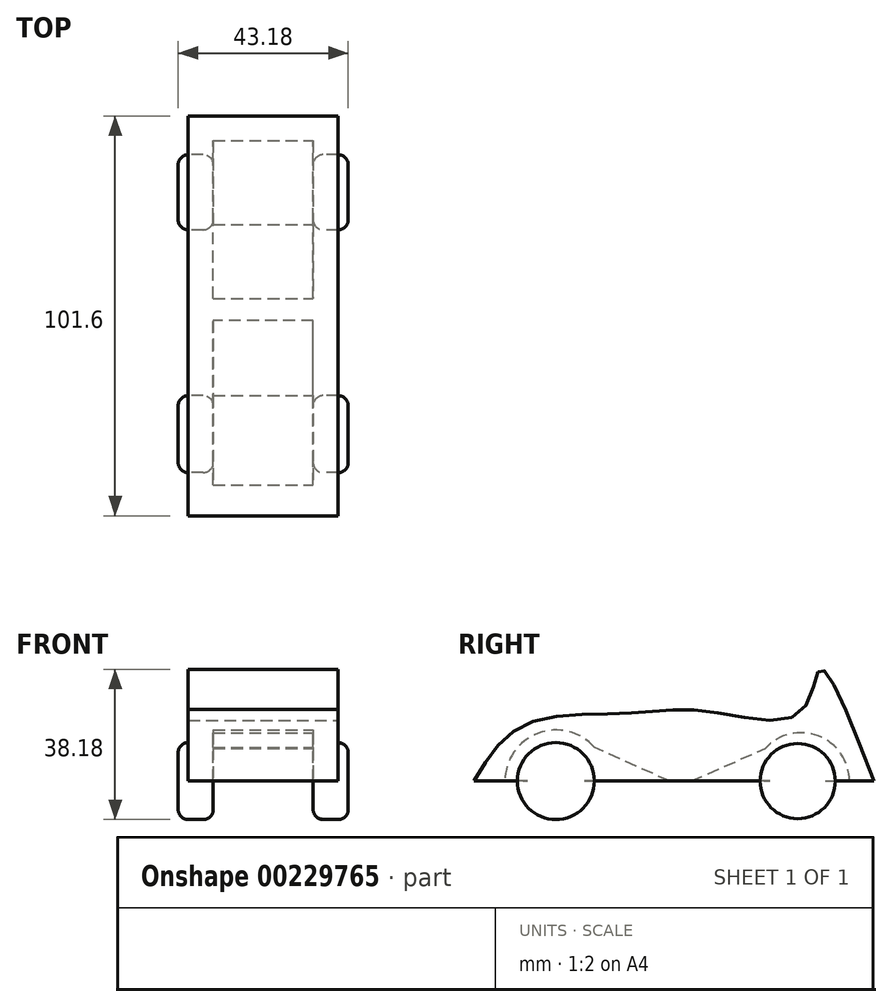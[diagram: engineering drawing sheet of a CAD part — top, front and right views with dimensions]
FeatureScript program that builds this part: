
annotation { "Feature Type Name" : "Feature", "Feature Type Description" : "" }
export const myFeature = defineFeature(function(context is Context, id is Id, definition is map)
    precondition{}
    {
        {
            var Q0;
            Q0=qCreatedBy(makeId("Right.planeOp"),FACE);
            var sketch = newSketch(context, id + "F0", { "sketchPlane" : qUnion([Q0])});
            skFitSpline(sketch, "E0", {"points": [v(-39.12, 0) * mm, v(-26.28, 14.3) * mm, v(0, 17.23) * mm, v(19.56, 17.8) * mm, v(43.8, 17.52) * mm, v(48.76, 28.32) * mm, v(62.48, 0) * mm], "startDerivative": vector(64.44, 109.87) * mm, "endDerivative": vector(84.94, -221.55) * mm});
            skLineSegment(sketch, "E1", {"start": v(-39.12, 0) * mm, "end": v(62.48, 0) * mm});
            skSolve(sketch);
        }
        {
            var Q0;
            Q0=qCreatedBy(makeId("Right.planeOp"),FACE);
            var sketch = newSketch(context, id + "F1", { "sketchPlane" : qUnion([Q0])});
            skCircle(sketch, "E2", {"center": v(-18.37, 0) * mm, "radius": 9.78 * mm});
            skCircle(sketch, "E3", {"center": v(43.09, 0) * mm, "radius": 9.55 * mm});
            skSolve(sketch);
        }
        {
            var Q0;
            Q0=makeQuery(id+"F0.imprint","IMPRINT",FACE,{"disambiguationData":[TD([[makeQuery(id+"F0.imprint","IMPRINT",EDGE,{"derivedFrom":sQuery(id+"F0.wireOp",EDGE,"E0")}),-1.0]])]});
            extrude(context, id + "F2", {"entities" : qUnion([Q0]), "endBound" : BoundingType.SYMMETRIC, "depth" : 38.1 * mm});
        }
        {
            var Q0;
            Q0=makeQuery(id+"F1.imprint","IMPRINT",FACE,{"disambiguationData":[TD([[makeQuery(id+"F1.imprint","IMPRINT",EDGE,{"derivedFrom":sQuery(id+"F1.wireOp",EDGE,"E2")}),1.0]])]});
            var Q1;
            Q1=makeQuery(id+"F1.imprint","IMPRINT",FACE,{"disambiguationData":[TD([[makeQuery(id+"F1.imprint","IMPRINT",EDGE,{"derivedFrom":sQuery(id+"F1.wireOp",EDGE,"E3")}),1.0]])]});
            extrude(context, id + "F3", {"entities" : qUnion([Q0, Q1]), "operationType" : NewBodyOperationType.ADD, "endBound" : BoundingType.SYMMETRIC, "depth" : 43.18 * mm});
        }
        {
            var Q0;
            Q0=makeQuery(id+"F3.opExtrude","CAP_EDGE",EDGE,{"disambiguationData":[OSD([sQuery(id+"F1.wireOp",EDGE,"E2")])],"isStart":false});
            var Q1;
            Q1=makeQuery(id+"F3.opExtrude","CAP_EDGE",EDGE,{"disambiguationData":[OSD([sQuery(id+"F1.wireOp",EDGE,"E3")])],"isStart":false});
            var Q2;
            Q2=makeQuery(id+"F3.opExtrude","CAP_EDGE",EDGE,{"disambiguationData":[OSD([sQuery(id+"F1.wireOp",EDGE,"E2")])],"isStart":true});
            var Q3;
            Q3=makeQuery(id+"F3.opExtrude","CAP_EDGE",EDGE,{"disambiguationData":[OSD([sQuery(id+"F1.wireOp",EDGE,"E3")])],"isStart":true});
            fillet(context, id + "F4", {"entities" : qUnion([Q0, Q1, Q2, Q3]), "radius" : 2.54 * mm, "tangentPropagation" : true, "allowEdgeOverflow" : false});
        }
        {
            var Q0;
            Q0=qCreatedBy(makeId("Right.planeOp"),FACE);
            var sketch = newSketch(context, id + "F5", { "sketchPlane" : qUnion([Q0])});
            skCircle(sketch, "E4", {"center": v(-18.29, 0) * mm, "radius": 12.97 * mm});
            skCircle(sketch, "E5", {"center": v(43.92, 0) * mm, "radius": 12.29 * mm});
            skSolve(sketch);
        }
        {
            var Q0;
            Q0=makeQuery(id+"F5.imprint","IMPRINT",FACE,{"disambiguationData":[TD([[makeQuery(id+"F5.imprint","IMPRINT",EDGE,{"derivedFrom":sQuery(id+"F5.wireOp",EDGE,"E5")}),1.0]])]});
            var Q1;
            Q1=makeQuery(id+"F5.imprint","IMPRINT",FACE,{"disambiguationData":[TD([[makeQuery(id+"F5.imprint","IMPRINT",EDGE,{"derivedFrom":sQuery(id+"F5.wireOp",EDGE,"E4")}),1.0]])]});
            extrude(context, id + "F6", {"entities" : qUnion([Q0, Q1]), "operationType" : NewBodyOperationType.REMOVE, "endBound" : BoundingType.SYMMETRIC, "oppositeDirection" : true, "depth" : 25.4 * mm});
        }
        {
            var Q0;
            {var subQ0=sQuery(id+"F0.wireOp",EDGE,"E1");var subQ1=sQuery(id+"F0.wireOp",EDGE,"E0");Q0=makeQuery(id+"F6.boolean.opBoolean","INTERSECT",EDGE,{"derivedFrom":[makeQuery(id+"F3.boolean.opBoolean","SPLIT",FACE,{"disambiguationData":[TD([makeQuery(id+"F2.opExtrude","CAP_FACE",FACE,{"disambiguationData":[OSD([subQ1,subQ0])],"isStart":true}),makeQuery(id+"F2.opExtrude","CAP_FACE",FACE,{"disambiguationData":[OSD([subQ1,subQ0])],"isStart":false}),makeQuery(id+"F3.opExtrude","SWEPT_FACE",FACE,{"disambiguationData":[OSD([sQuery(id+"F1.wireOp",EDGE,"E2")])]}),makeQuery(id+"F3.opExtrude","SWEPT_FACE",FACE,{"disambiguationData":[OSD([sQuery(id+"F1.wireOp",EDGE,"E3")])]})])],"derivedFrom":makeQuery(id+"F2.opExtrude","SWEPT_FACE",FACE,{"disambiguationData":[OSD([subQ0])]})}),makeQuery(id+"F6.opExtrude","SWEPT_FACE",FACE,{"disambiguationData":[OSD([sQuery(id+"F5.wireOp",EDGE,"E5")])]})]});}
            var Q1;
            {var subQ0=sQuery(id+"F0.wireOp",EDGE,"E1");var subQ1=sQuery(id+"F0.wireOp",EDGE,"E0");Q1=makeQuery(id+"F6.boolean.opBoolean","INTERSECT",EDGE,{"derivedFrom":[makeQuery(id+"F3.boolean.opBoolean","SPLIT",FACE,{"disambiguationData":[TD([makeQuery(id+"F2.opExtrude","CAP_FACE",FACE,{"disambiguationData":[OSD([subQ1,subQ0])],"isStart":true}),makeQuery(id+"F2.opExtrude","CAP_FACE",FACE,{"disambiguationData":[OSD([subQ1,subQ0])],"isStart":false}),makeQuery(id+"F3.opExtrude","SWEPT_FACE",FACE,{"disambiguationData":[OSD([sQuery(id+"F1.wireOp",EDGE,"E2")])]}),makeQuery(id+"F3.opExtrude","SWEPT_FACE",FACE,{"disambiguationData":[OSD([sQuery(id+"F1.wireOp",EDGE,"E3")])]})])],"derivedFrom":makeQuery(id+"F2.opExtrude","SWEPT_FACE",FACE,{"disambiguationData":[OSD([subQ0])]})}),makeQuery(id+"F6.opExtrude","SWEPT_FACE",FACE,{"disambiguationData":[OSD([sQuery(id+"F5.wireOp",EDGE,"E4")])]})]});}
            chamfer(context, id + "F7", {"entities" : qUnion([Q0, Q1]), "width" : 25.4 * mm, "tangentPropagation" : true});
        }
        {
            var Q0;
            Q0=makeQuery(id+"F6.boolean.opBoolean","INTERSECT",EDGE,{"derivedFrom":[makeQuery(id+"F3.opExtrude","SWEPT_FACE",FACE,{"disambiguationData":[OSD([sQuery(id+"F1.wireOp",EDGE,"E3")])]}),makeQuery(id+"F6.opExtrude","CAP_FACE",FACE,{"disambiguationData":[OSD([sQuery(id+"F5.wireOp",EDGE,"E5")])],"isStart":false})]});
            var Q1;
            Q1=makeQuery(id+"F6.boolean.opBoolean","INTERSECT",EDGE,{"derivedFrom":[makeQuery(id+"F3.opExtrude","SWEPT_FACE",FACE,{"disambiguationData":[OSD([sQuery(id+"F1.wireOp",EDGE,"E2")])]}),makeQuery(id+"F6.opExtrude","CAP_FACE",FACE,{"disambiguationData":[OSD([sQuery(id+"F5.wireOp",EDGE,"E4")])],"isStart":false})]});
            var Q2;
            Q2=makeQuery(id+"F6.boolean.opBoolean","INTERSECT",EDGE,{"derivedFrom":[makeQuery(id+"F3.opExtrude","SWEPT_FACE",FACE,{"disambiguationData":[OSD([sQuery(id+"F1.wireOp",EDGE,"E3")])]}),makeQuery(id+"F6.opExtrude","CAP_FACE",FACE,{"disambiguationData":[OSD([sQuery(id+"F5.wireOp",EDGE,"E5")])],"isStart":true})]});
            var Q3;
            Q3=makeQuery(id+"F6.boolean.opBoolean","INTERSECT",EDGE,{"derivedFrom":[makeQuery(id+"F3.opExtrude","SWEPT_FACE",FACE,{"disambiguationData":[OSD([sQuery(id+"F1.wireOp",EDGE,"E2")])]}),makeQuery(id+"F6.opExtrude","CAP_FACE",FACE,{"disambiguationData":[OSD([sQuery(id+"F5.wireOp",EDGE,"E4")])],"isStart":true})]});
            fillet(context, id + "F8", {"entities" : qUnion([Q0, Q1, Q2, Q3]), "radius" : 2.54 * mm, "tangentPropagation" : true, "allowEdgeOverflow" : false});
        }
    });
